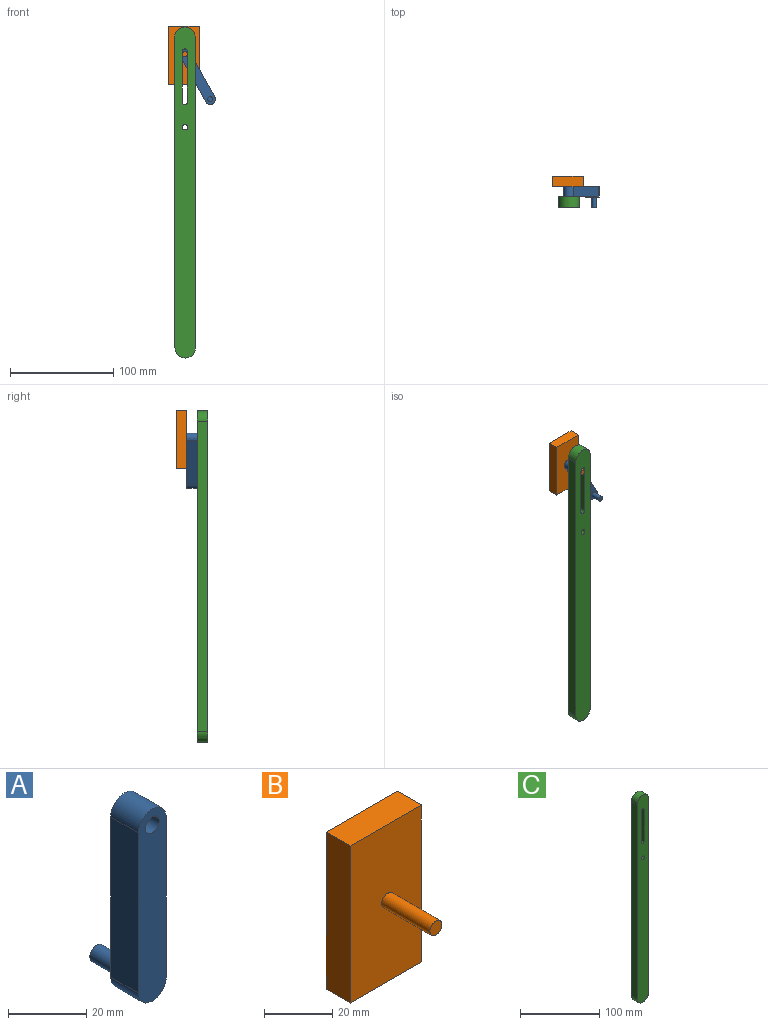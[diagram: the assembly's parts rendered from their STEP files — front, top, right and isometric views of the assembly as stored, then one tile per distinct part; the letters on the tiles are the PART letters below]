
ASSEMBLY  parts=3 mates=2
PART A: 9 faces, bbox 10x20x60 mm
  f0: cylinder r=5mm len=10mm, axis (0,1,0), area 157.1mm2, adj f1,f3,f5,f6
  f1: plane 50x10mm, normal (-1,0,0), area 500mm2, adj f0,f2,f5,f6
  f2: cylinder r=5mm len=10mm, axis (0,1,0), area 157.1mm2, adj f1,f3,f5,f6
  f3: plane 50x10mm, normal (1,0,0), area 500mm2, adj f0,f2,f5,f6
  f4: cylinder r=2.5mm len=10mm, axis (0,1,0), area 157.1mm2, adj f5,f6
  f5: plane 60x10mm, normal (0,-1,0), area 558.9mm2, adj f0,f1,f2,f3,f4
  f6: plane 60x10mm, normal (0,1,0), area 539.3mm2, adj f0,f1,f2,f3,f4,f7
  f7: cylinder r=2.5mm len=10mm, axis (0,-1,0), area 157.1mm2, adj f6,f8
  f8: plane 5x5mm, normal (0,1,0), area 19.6mm2, adj f7
PART B: 8 faces, bbox 29.6x30x56.4 mm
  f0: plane 29.56x10mm, normal (0,0,1), area 295.6mm2, adj f1,f3,f4,f5
  f1: plane 56.41x10mm, normal (-1,0,0), area 564.1mm2, adj f0,f2,f4,f5
  f2: plane 29.56x10mm, normal (0,0,-1), area 295.6mm2, adj f1,f3,f4,f5
  f3: plane 56.41x10mm, normal (1,0,0), area 564.1mm2, adj f0,f2,f4,f5
  f4: plane 56.41x29.56mm, normal (0,-1,0), area 1647.7mm2, adj f0,f1,f2,f3,f6
  f5: plane 56.41x29.56mm, normal (0,1,0), area 1667.3mm2, adj f0,f1,f2,f3
  f6: cylinder r=2.5mm len=20mm, axis (0,1,0), area 314.2mm2, adj f4,f7
  f7: plane 5x5mm, normal (0,-1,0), area 19.6mm2, adj f6
PART C: 11 faces, bbox 20x10x320 mm
  f0: cylinder r=2.5mm len=10mm, axis (0,1,0), area 78.5mm2, adj f1,f6,f9,f10
  f1: plane 49.07x10mm, normal (1,0,0), area 490.7mm2, adj f0,f2,f9,f10
  f2: cylinder r=2.5mm len=10mm, axis (0,1,0), area 78.5mm2, adj f1,f6,f9,f10
  f3: cylinder r=10mm len=20mm, axis (0,1,0), area 314.2mm2, adj f4,f7,f9,f10
  f4: plane 300x10mm, normal (-1,0,0), area 3000mm2, adj f3,f5,f9,f10
  f5: cylinder r=10mm len=20mm, axis (0,1,0), area 314.2mm2, adj f4,f7,f9,f10
  f6: plane 49.07x10mm, normal (-1,0,0), area 490.7mm2, adj f0,f2,f9,f10
  f7: plane 300x10mm, normal (1,0,0), area 3000mm2, adj f3,f5,f9,f10
  f8: cylinder r=2.63mm len=10mm, axis (0,1,0), area 165mm2, adj f9,f10
  f9: plane 320x20mm, normal (0,-1,0), area 6027.5mm2, adj f0,f1,f2,f3,f4,f5,f6,f7
  f10: plane 320x20mm, normal (0,1,0), area 6027.5mm2, adj f0,f1,f2,f3,f4,f5,f6,f7
PLACE A rot(axis=(0.25,0,-0.97),180deg) t=(0.95,-20,-38.48)mm
PLACE B at identity fixed
PLACE C rot(axis=(0,-1,0),0.1deg) t=(-91.47,-20,-240.23)mm
MATE revolute B.f6 <-> A.f0  axis (0,1,0) through (-31.49,-10,4.54)mm
MATE pin_slot B.f6 <-> C.f0  axis (0,-1,0) through (-31.49,-30,4.54)mm
